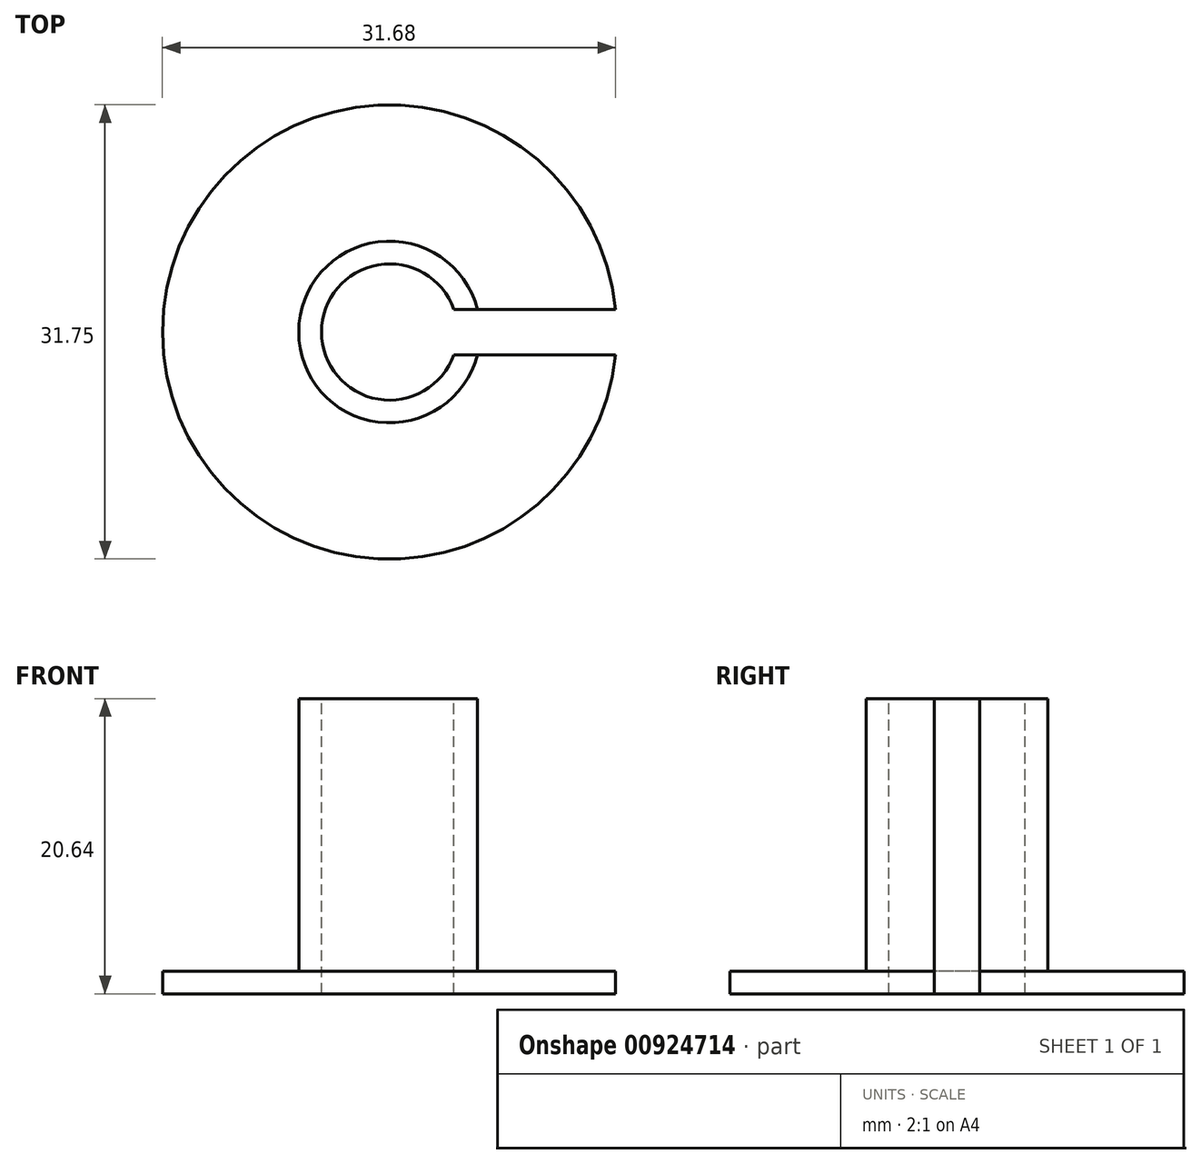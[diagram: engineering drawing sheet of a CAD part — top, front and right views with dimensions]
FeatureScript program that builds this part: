
annotation { "Feature Type Name" : "Feature", "Feature Type Description" : "" }
export const myFeature = defineFeature(function(context is Context, id is Id, definition is map)
    precondition{}
    {
        {
            var Q0;
            Q0=qCreatedBy(makeId("Top.planeOp"),FACE);
            var sketch = newSketch(context, id + "F0", { "sketchPlane" : qUnion([Q0])});
            skCircle(sketch, "E0", {"center": v(0, 0) * mm, "radius": 15.88 * mm});
            skSolve(sketch);
        }
        {
            var Q0;
            Q0=makeQuery(id+"F0.imprint","IMPRINT",FACE,{"disambiguationData":[TD([[makeQuery(id+"F0.imprint","IMPRINT",EDGE,{"derivedFrom":sQuery(id+"F0.wireOp",EDGE,"E0")}),1.0]])]});
            extrude(context, id + "F1", {"entities" : qUnion([Q0]), "depth" : 1.59 * mm, "offsetDistance" : 25.4 * mm});
        }
        {
            var Q0;
            Q0=makeQuery(id+"F1.opExtrude","CAP_FACE",FACE,{"disambiguationData":[OSD([sQuery(id+"F0.wireOp",EDGE,"E0")])],"isStart":false});
            var sketch = newSketch(context, id + "F2", { "sketchPlane" : qUnion([Q0])});
            skCircle(sketch, "E1", {"center": v(0, 0) * mm, "radius": 6.35 * mm});
            skSolve(sketch);
        }
        {
            var Q0;
            Q0 = qSketchRegion(id + "F2", true);
            extrude(context, id + "F3", {"entities" : qUnion([Q0]), "operationType" : NewBodyOperationType.ADD, "depth" : 19.05 * mm, "offsetDistance" : 25.4 * mm});
        }
        {
            var Q0;
            Q0=makeQuery(id+"F3.opExtrude","CAP_FACE",FACE,{"disambiguationData":[OSD([sQuery(id+"F2.wireOp",EDGE,"E1")])],"isStart":false});
            var sketch = newSketch(context, id + "F4", { "sketchPlane" : qUnion([Q0])});
            skArc(sketch, "E2", {"start": v(4.5, 1.59) * mm, "mid": v(-4.76, 0) * mm, "end": v(4.5, -1.59) * mm});
            skLineSegment(sketch, "E3", {"start": v(15.8, 1.59) * mm, "end": v(4.5, 1.59) * mm});
            skLineSegment(sketch, "E4", {"start": v(15.8, -1.59) * mm, "end": v(4.5, -1.59) * mm});
            skArc(sketch, "E5", {"start": v(15.8, -1.59) * mm, "mid": v(15.88, 0) * mm, "end": v(15.8, 1.59) * mm});
            skSolve(sketch);
        }
        {
            var Q0;
            Q0 = qSketchRegion(id + "F4", true);
            extrude(context, id + "F5", {"entities" : qUnion([Q0]), "operationType" : NewBodyOperationType.REMOVE, "endBound" : BoundingType.THROUGH_ALL, "oppositeDirection" : true, "depth" : 25.4 * mm, "offsetDistance" : 25.4 * mm});
        }
    });
